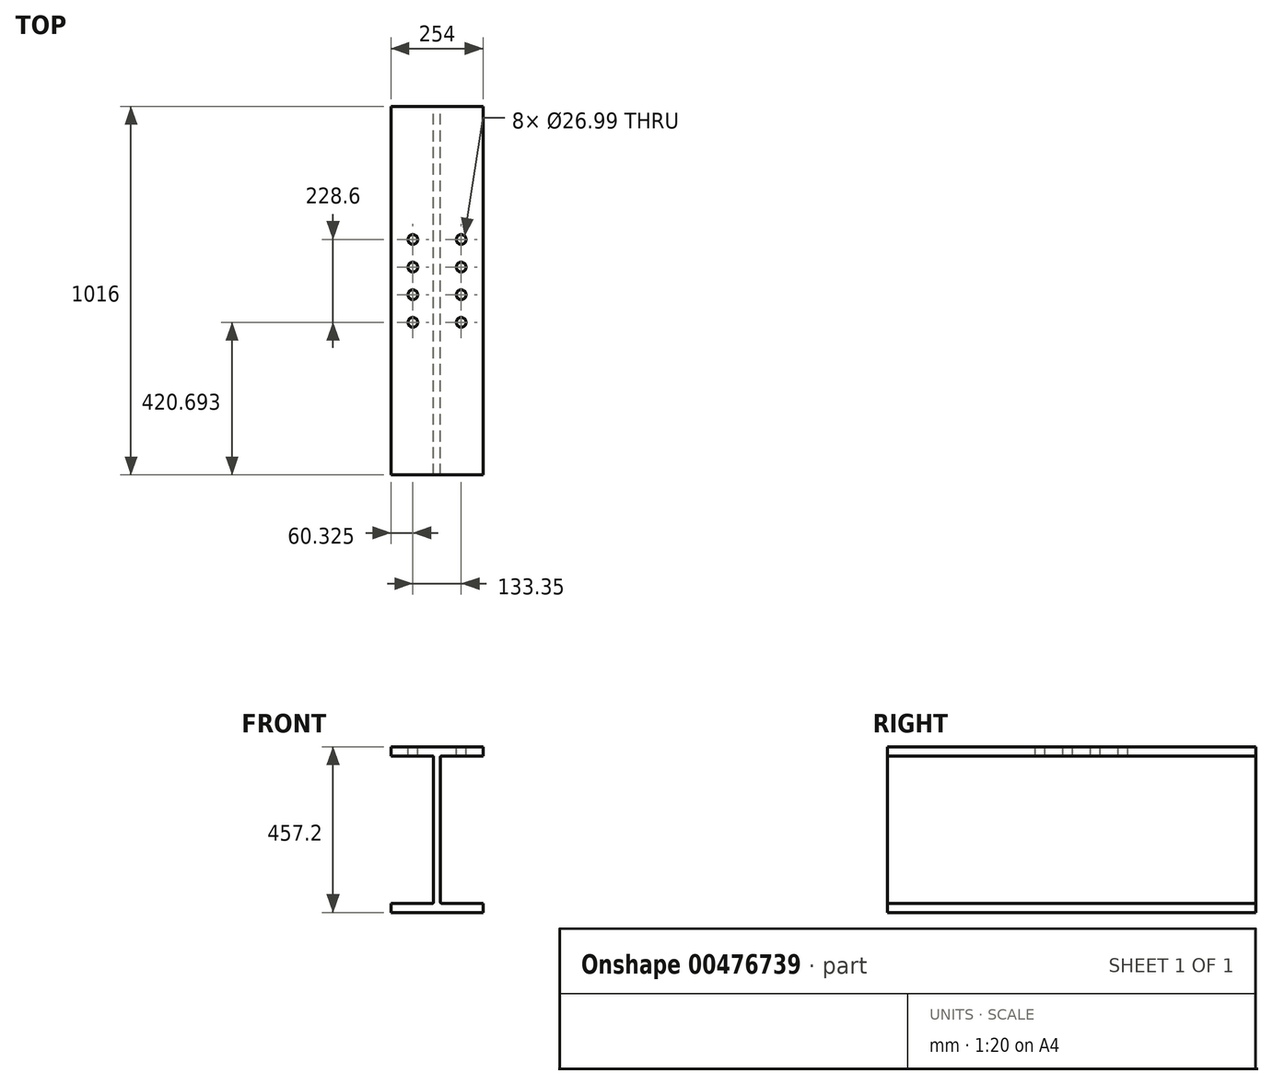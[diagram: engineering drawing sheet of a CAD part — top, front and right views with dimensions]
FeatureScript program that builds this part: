
annotation { "Feature Type Name" : "Feature", "Feature Type Description" : "" }
export const myFeature = defineFeature(function(context is Context, id is Id, definition is map)
    precondition{}
    {
        {
            var Q0;
            Q0=qCreatedBy(makeId("Front.planeOp"),FACE);
            var sketch = newSketch(context, id + "F0", { "sketchPlane" : qUnion([Q0])});
            skLineSegment(sketch, "E0", {"start": v(127, -203.2) * mm, "end": v(12.06, -203.2) * mm});
            skLineSegment(sketch, "E1", {"start": v(9.52, -200.66) * mm, "end": v(9.52, 200.66) * mm});
            skLineSegment(sketch, "E2", {"start": v(12.06, 203.2) * mm, "end": v(127, 203.2) * mm});
            skLineSegment(sketch, "E3", {"start": v(-127, 203.2) * mm, "end": v(-12.06, 203.2) * mm});
            skLineSegment(sketch, "E4", {"start": v(-9.53, 200.66) * mm, "end": v(-9.53, -200.66) * mm});
            skLineSegment(sketch, "E5", {"start": v(-12.06, -203.2) * mm, "end": v(-127, -203.2) * mm});
            skLineSegment(sketch, "E6", {"start": v(0, 0) * mm, "end": v(-9.52, 0) * mm, "construction": true});
            skLineSegment(sketch, "E7", {"start": v(0, 0) * mm, "end": v(9.52, 0) * mm, "construction": true});
            skLineSegment(sketch, "E8", {"start": v(0, 0) * mm, "end": v(0, 228.6) * mm, "construction": true});
            skLineSegment(sketch, "E9", {"start": v(0, 0) * mm, "end": v(0, -228.6) * mm, "construction": true});
            skPoint(sketch, "E10.visualSharp", {"position": v(-9.53, 203.2) * mm});
            skArc(sketch, "E10.filletArc", {"start": v(-9.52, 200.66) * mm, "mid": v(-10.27, 202.46) * mm, "end": v(-12.06, 203.2) * mm});
            skPoint(sketch, "E11.visualSharp", {"position": v(9.53, 203.2) * mm});
            skArc(sketch, "E11.filletArc", {"start": v(12.06, 203.2) * mm, "mid": v(10.27, 202.46) * mm, "end": v(9.52, 200.66) * mm});
            skPoint(sketch, "E12.visualSharp", {"position": v(9.53, -203.2) * mm});
            skArc(sketch, "E12.filletArc", {"start": v(9.52, -200.66) * mm, "mid": v(10.27, -202.46) * mm, "end": v(12.06, -203.2) * mm});
            skPoint(sketch, "E13.visualSharp", {"position": v(-9.53, -203.2) * mm});
            skArc(sketch, "E13.filletArc", {"start": v(-12.06, -203.2) * mm, "mid": v(-10.27, -202.46) * mm, "end": v(-9.52, -200.66) * mm});
            skPoint(sketch, "E14.visualSharp", {"position": v(-127, 228.6) * mm});
            skPoint(sketch, "E15.visualSharp", {"position": v(127, 228.6) * mm});
            skPoint(sketch, "E16.visualSharp", {"position": v(127, 203.2) * mm});
            skPoint(sketch, "E17.visualSharp", {"position": v(127, -228.6) * mm});
            skPoint(sketch, "E18.visualSharp", {"position": v(-127, -203.2) * mm});
            skPoint(sketch, "E19.visualSharp", {"position": v(-127, -228.6) * mm});
            skLineSegment(sketch, "E20", {"start": v(127, -203.2) * mm, "end": v(127, -228.6) * mm});
            skLineSegment(sketch, "E21", {"start": v(-127, -203.2) * mm, "end": v(-127, -228.6) * mm});
            skLineSegment(sketch, "E22", {"start": v(-127, 228.6) * mm, "end": v(-127, 203.2) * mm});
            skLineSegment(sketch, "E23", {"start": v(127, 228.6) * mm, "end": v(127, 203.2) * mm});
            skLineSegment(sketch, "E24", {"start": v(-127, 228.6) * mm, "end": v(127, 228.6) * mm});
            skLineSegment(sketch, "E25", {"start": v(-127, -228.6) * mm, "end": v(127, -228.6) * mm});
            skSolve(sketch);
        }
        {
            var Q0;
            Q0=makeQuery(id+"F0.imprint","IMPRINT",FACE,{"disambiguationData":[TD([[makeQuery(id+"F0.imprint","IMPRINT",EDGE,{"derivedFrom":sQuery(id+"F0.wireOp",EDGE,"E0")}),1.0]])]});
            extrude(context, id + "F1", {"entities" : qUnion([Q0]), "endBound" : BoundingType.SYMMETRIC, "depth" : 1016 * mm});
        }
        {
            var Q0;
            Q0=makeQuery(id+"F1.opExtrude","SWEPT_FACE",FACE,{"disambiguationData":[OSD([sQuery(id+"F0.wireOp",EDGE,"E24")])]});
            var sketch = newSketch(context, id + "F2", { "sketchPlane" : qUnion([Q0])});
            skPoint(sketch, "E26", {"position": v(-66.68, 141.3) * mm});
            skPoint(sketch, "E27", {"position": v(-66.68, 65.1) * mm});
            skPoint(sketch, "E28", {"position": v(-66.68, -11.1) * mm});
            skPoint(sketch, "E29", {"position": v(-66.68, -87.3) * mm});
            skPoint(sketch, "E30", {"position": v(66.67, 141.3) * mm});
            skPoint(sketch, "E31", {"position": v(66.67, 65.1) * mm});
            skPoint(sketch, "E32", {"position": v(66.67, -11.1) * mm});
            skPoint(sketch, "E33", {"position": v(66.67, -87.3) * mm});
            skSolve(sketch);
        }
        {
            var Q0;
            Q0=sQuery(id+"F2.wireOp",VERTEX,"E26");
            var Q1;
            Q1=sQuery(id+"F2.wireOp",VERTEX,"E27");
            var Q2;
            Q2=sQuery(id+"F2.wireOp",VERTEX,"E28");
            var Q3;
            Q3=sQuery(id+"F2.wireOp",VERTEX,"E29");
            var Q4;
            Q4=sQuery(id+"F2.wireOp",VERTEX,"E33");
            var Q5;
            Q5=sQuery(id+"F2.wireOp",VERTEX,"E32");
            var Q6;
            Q6=sQuery(id+"F2.wireOp",VERTEX,"E31");
            var Q7;
            Q7=sQuery(id+"F2.wireOp",VERTEX,"E30");
            var Q8;
            Q8=makeQuery(id+"F1.opExtrude","SWEPT_BODY",BODY,{"disambiguationData":[OSD([sQuery(id+"F0.wireOp",EDGE,"E0"),sQuery(id+"F0.wireOp",EDGE,"E1"),sQuery(id+"F0.wireOp",EDGE,"E2"),sQuery(id+"F0.wireOp",EDGE,"E3"),sQuery(id+"F0.wireOp",EDGE,"E4"),sQuery(id+"F0.wireOp",EDGE,"E5"),sQuery(id+"F0.wireOp",EDGE,"E10.filletArc"),sQuery(id+"F0.wireOp",EDGE,"E11.filletArc"),sQuery(id+"F0.wireOp",EDGE,"E12.filletArc"),sQuery(id+"F0.wireOp",EDGE,"E13.filletArc"),sQuery(id+"F0.wireOp",EDGE,"E20"),sQuery(id+"F0.wireOp",EDGE,"E21"),sQuery(id+"F0.wireOp",EDGE,"E22"),sQuery(id+"F0.wireOp",EDGE,"E23"),sQuery(id+"F0.wireOp",EDGE,"E24"),sQuery(id+"F0.wireOp",EDGE,"E25")])]});
            hole(context, id + "F3", {"style" : HoleStyle.SIMPLE, "endStyle" : HoleEndStyle.BLIND, "holeDiameter" : 26.99 * mm, "holeDepth" : 25.4 * mm, "isTappedThrough" : true, "tappedDepth" : 12.7 * mm, "tapClearance" : 3, "locations" : qUnion([Q0, Q1, Q2, Q3, Q4, Q5, Q6, Q7]), "scope" : qUnion([Q8])});
        }
    });
